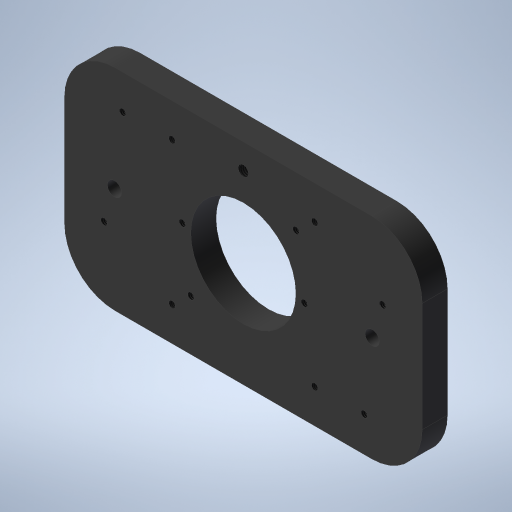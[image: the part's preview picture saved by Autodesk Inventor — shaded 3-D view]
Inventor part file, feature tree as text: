
AUTODESK INVENTOR PART (.ipt)
format: ipt  version: 2024 (Build 280153000, 153)  size: 283,136 bytes
history: native  units: in
note: dims shown in document units (in); Inventor stores cm internally (conversion verified against a paired STEP export)
features: hole x5, sketch x2, extrude x1
ambient origin geometry x8: Origin, YZ Plane, XZ Plane, XY Plane, X Axis, Y Axis, Z Axis, Center Point
bodies: Solid1 (feature_tree)
feature tree (8):
  sketch  "Sketch1"  dims[d0=3.3465in d1=1.9685in]
  extrude  "Extrusion1"  Depth=1.9685in
  hole  "Hole1"  [1 undecoded]
  hole  "Hole2"  [1 undecoded]
  hole  "Hole3"  [1 undecoded]
  hole  "Hole4"  [1 undecoded]
  hole  "Hole5"  [1 undecoded]
  sketch  "Sketch2"  dims[d2=0.4724in d3=1.5in d4=1.5in d5=0.9843in d6=0.0827in d7=0.0827in d8=0.1772in d9=0.0827in d10=0.0827in d11=0.0827in d12=0.0827in d13=0.0827in d14=0.0827in d15=0.1772in d16=0.1772in d17=0.1772in d18=1.2057in d19=1.2057in d20=0.252in d21=0.252in d22=0.2244in d23=0.2362in d24=0.0in d25=0.1339in d26=0.2362in d27=0.3701in d28=0.0787in d29=90.0deg d30=0.3346in d31=0.8108in d32=0.0968in d33=0.2362in d34=0.1575in d35=0.0787in d36=90.0deg d37=0.3465in d38=0.8108in d39=0.0617in d40=0.1575in d41=0.1575in d42=0.0787in d43=90.0deg d44=0.248in d45=0.8108in d46=0.9843in d47=0.1575in d48=0.1575in d49=0.0787in d50=90.0deg d51=0.248in d52=0.8108in d53=1.1024in d54=0.9449in d55=0.3256in d56=0.5433in d57=0.3256in d58=0.5433in d59=1.1024in d60=0.9449in d61=1.1811in d62=0.4724in d63=1.1811in d64=0.4724in d65=0.6693in d66=0.3697in d67=0.6693in d68=0.3697in d69=0.0617in d70=0.1575in d71=0.1575in d72=0.0787in d73=90.0deg d74=0.248in d75=0.8108in]
note: 5 required parameter values undecoded (feature->parameter linkage not recoverable at this tier; creation-order binding heuristic only, values carry confidence <= 0.55)
